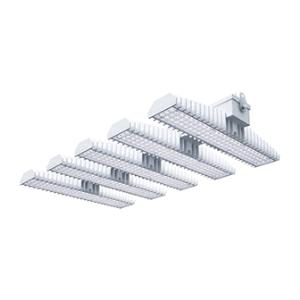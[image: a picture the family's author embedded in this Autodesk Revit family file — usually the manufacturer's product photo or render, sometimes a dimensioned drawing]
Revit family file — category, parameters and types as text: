
# Revit family: 3f_filippi_-_3f_lem_medio_3f_filippi_-_58897_a0811_-_3f_lem_5_led_250_cr_medio___vt_b36e
name_source: partatom
category: Lighting Fixtures
units: mm (PartAtom-declared; Revit-internal decimal feet)

## family parameters
Cut with Voids When Loaded = No
Host = Face
Light Source = No
Part Type = Normal
Room Calculation Point = No
Round Connector Dimension = Use Diameter
Shared = No

## types (1)
- 3F Filippi - 3F LEM Medio (1 x LED, 38698 lm, 274 W, 4000 K)
    Apparent Load = 274 VA
    Approval mark = CE
    CIE Flux Codes = 83 96 99 100 100
    Color Rendering = 80
    Color Temperature = 4000 K
    Control Gear = Electronic ballast
    Default Elevation = 1800 mm
    Description = Industrial luminaire with high light output and high luminous efficiency designed with the most innovative technologies for environments with temperature up to 55°C.

ILLUMINOTECHNICAL
Luminous efficiency 100% (DLOR 99%, ULOR 1%).
Initial luminous flux of the luminaire 38698 lm.
Medium distribution with rectangular shape.
Installation Interdistance Transv.D = 1.02 x hu - Long.D = 1.06 x hu.
Tabular UGR (CIE 117 - 4H-8H; S=0.25H; 70/50/20): RUG 18.9 - 18.5.
Beam angle: 65° - 67°.
Luminous efficacy 141 lm/W.
Lifetime (L93/B10): 30000 h. (tq+25°C)
Lifetime (L90/B10): 50000 h. (tq+25°C)
Lifetime (L85/B10): 80000 h. (tq+25°C)
Lifetime (L80/B10): 100000 h. (tq+25°C)
Lifetime (L85/B10): 50000 h. (tq+55°C)
Sudden decreased luminous flux after 50000 hours: 0% (C0).
Photobiological safety in compliance with IEC/TR 62778: RG0 risk exempt, (IEC 62471).
In compliance with IEC/EN 62722-2-1 - IEC/EN 62717 standards.

SOURCE
5 Mid-Power linear LED modules 50W/840.
Energy efficiency class (UE 2019/2020 - UE 2019/2015): C.
CIE 13.3 Colour rendering index: CRI >80 (R9 <50%).
IES TM-30 Fidelity Index: Rf = 84 Rg = 95.
CCT nominal colour temperature 4000 K.
Colour initial tolerance (MacAdam): SDCM 3.

MECHANICAL
Passive modular heatsinks in die-casted aluminium, painted in white colour.
To optimize the thermal management of the LED module, the heatsinks are oversized and provided with self-cleaning of cooling fins.
Wiring body in aluminium and galvanised steel anchored solidly to the sinks and thermally separated.
3F Lens lenses with high luminous efficiency, transparent methacrylate (PMMA), fixed to the LED modules.
Fixing brackets in stainless steel.
Luminaire with limited surface temperature. - D - (EN 60598-2-24)
Dimensions: 952x542 mm, height 133 mm. Weight 24.13 kg.
IP65 protection degree.
Mechanical strength to impacts IK06 (1 joule).
Glow-wire test resistance 650°C.

ELECTRICAL
Halogen Free electronic wiring 230V-50/60Hz, power factor 0.97, THD <25%, constant output current, class I, 3 driver.
Power of the luminaire 274 W.
ENEC - CE.
SAFE FLICKER: PstLM=<1 and SVM=<0.4 (IEC TR 61547-1 and IEC TR 63158), to ensure a more comfortable and safe light.
Luminaire compliant with EN 60598-2-22 for power supply from a centralised emergency system CPSS (Central Power Supply System), not incorporated in the luminaire - high risk areas excluded. The default power and flux are 100% in AC and 100% in DC.
Ambient temperature from -30°C to +55°C.
Temperature class T6 max 85°C.
Quick connection via M20 3P connector with 9-13 mm tightening range.
Power unit positioned on a separate compartment by the LED module to ensure optimum temperatures of cabling components, to be inspectable and maintainable.
Relative humidity UR: <85%.

INSTALLATION
Ceiling / Suspended / Wall.
All accessories dedicated to this product are available on the Catalog and on our website www.3F-Filippi.com.

ACCESSORIES
A0811 - VT transparent glass, tempered, not flammable, with sealing gasket.
One required for each light module. The pack contains 10 pieces.

APPLICATIONS
In commercial environments, exhibition and industrial areas, stores, open areas.
Applications with high ambient temperature up to 55°C.
Environments in which it is necessary a total protection against falling fragments (eg environments with foodstuffs or machines with moving parts or with extreme temperature changes), use luminaires with polycarbonate lenses.

WARNING
Fixture not suitable for cold stores with an ambient temperature <0°C and/or relative humidity >85%.
Luminaire designed for disposal/recycling at end-of-life.
Replaceable (LED only) light source by a professional. Replaceable control gear by a professional.
    Height = 133 mm  [stored 0.436352 ft]
    Lamp = 1 x LED
    Lamp Light Flux = 38698 lm
    Lamp Power = 274 W
    Lamp count = 1
    Length = 952 mm
    Lifetime = 50000 h
    Luminous efficacy = 141 lm/W
    Manufacturer = 3F Filippi
    ModVariant = No
    Model = 3F Filippi - 58897+A0811 - 3F LEM 5 LED 250 CR MEDIO + VT
    Mounting Place = Ceiling
    Mounting Type = Pendant
    Number of Poles = 1
    OnlyDefault = Yes
    Power Factor = 1
    Product Name = 3F Filippi - 3F LEM Medio
    Product group = pendant luminaire
    ProductGroupID = 9
    Protection Class = Protection class I
    Protection Degree = IP 65
    RLX_Detail_Level = 1
    RLX_Emergency_Light_Flux = 0 lm
    RLX_Emergency_Type = 0
    RLX_Emergency_Type_DB = No
    RlxData = <blob elided: 126893 chars, md5=01eb1531>
    Socket = socket
    Standby Power = 0 W
    System Light Flux = 38698 lm
    System Power = 274 W
    Type Comments = Product without accessories
    Type Image = 3f_filippi_-_lem_5__a0811.jpg
    URL = http://relux.com
    VarID = ---
    Voltage = 0 V
    Weight = 0.00 kg
    Width = 542 mm

note: [stored X ft] marks values corroborated as IEEE doubles in the binary element streams (Revit-internal decimal feet)

## geometry (parser evidence)
native form markers: Blend x4, Sweep x11
no freeform markers — native parametric forms only
